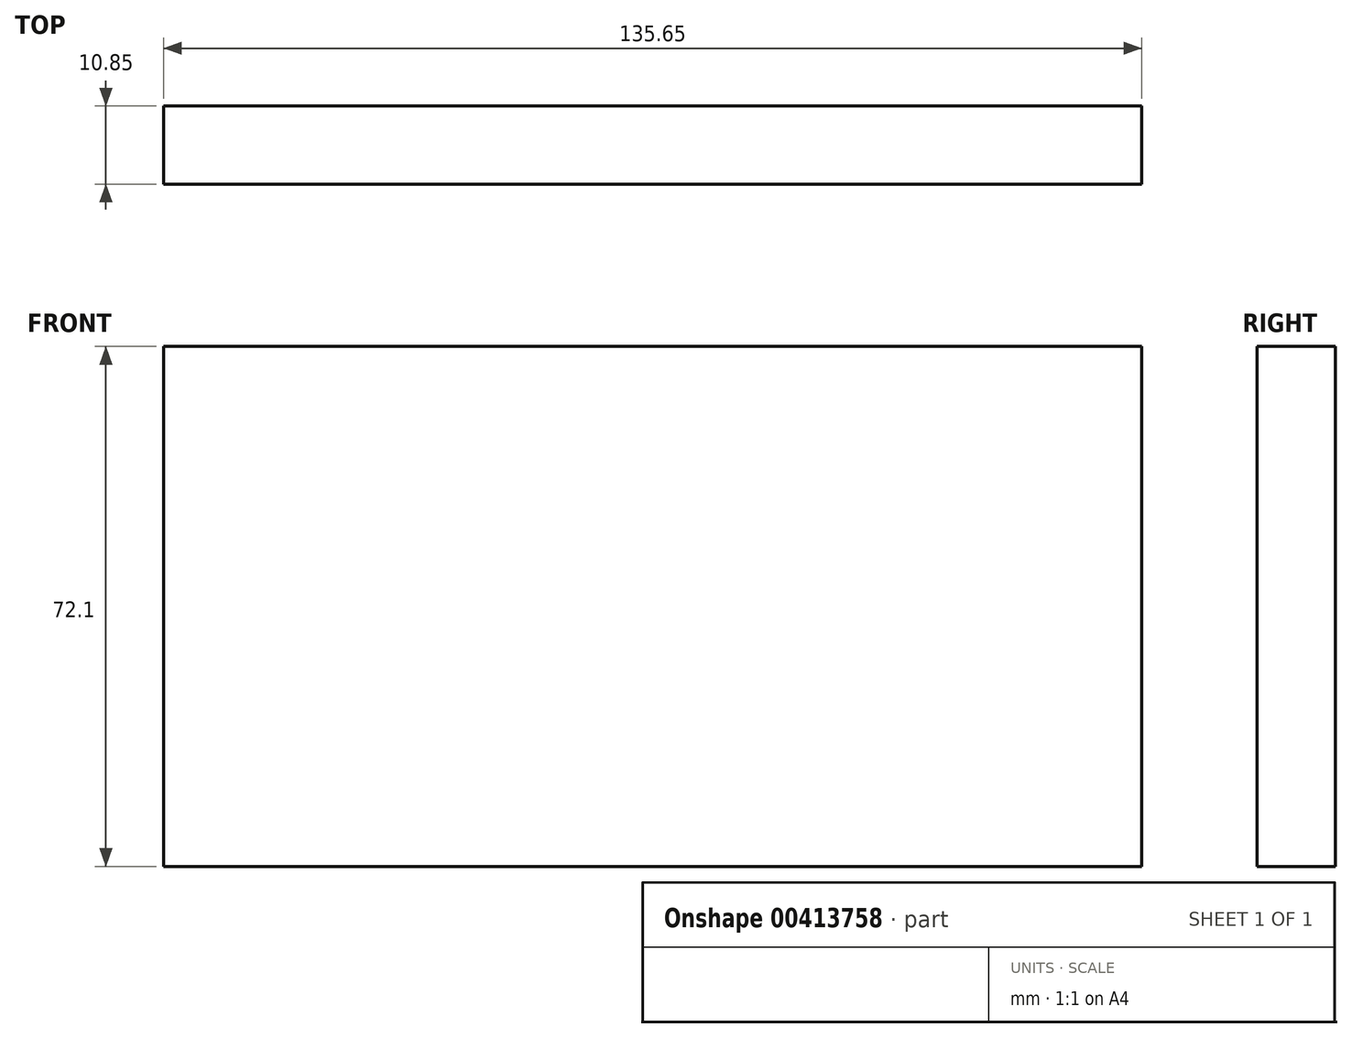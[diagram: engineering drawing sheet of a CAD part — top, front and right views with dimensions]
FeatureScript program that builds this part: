
annotation { "Feature Type Name" : "Feature", "Feature Type Description" : "" }
export const myFeature = defineFeature(function(context is Context, id is Id, definition is map)
    precondition{}
    {
        {
            var Q0;
            Q0=qCreatedBy(makeId("Front.planeOp"),FACE);
            var sketch = newSketch(context, id + "F0", { "sketchPlane" : qUnion([Q0])});
            skLineSegment(sketch, "E0.bottom", {"start": v(-66.48, 0) * mm, "end": v(69.17, 0) * mm});
            skLineSegment(sketch, "E0.top", {"start": v(-66.48, -72.1) * mm, "end": v(69.17, -72.1) * mm});
            skLineSegment(sketch, "E0.left", {"start": v(-66.48, 0) * mm, "end": v(-66.48, -72.1) * mm});
            skLineSegment(sketch, "E0.right", {"start": v(69.17, 0) * mm, "end": v(69.17, -72.1) * mm});
            skSolve(sketch);
        }
        {
            var Q0;
            Q0 = qSketchRegion(id + "F0", true);
            extrude(context, id + "F1", {"entities" : qUnion([Q0]), "depth" : 10.85 * mm});
        }
    });
